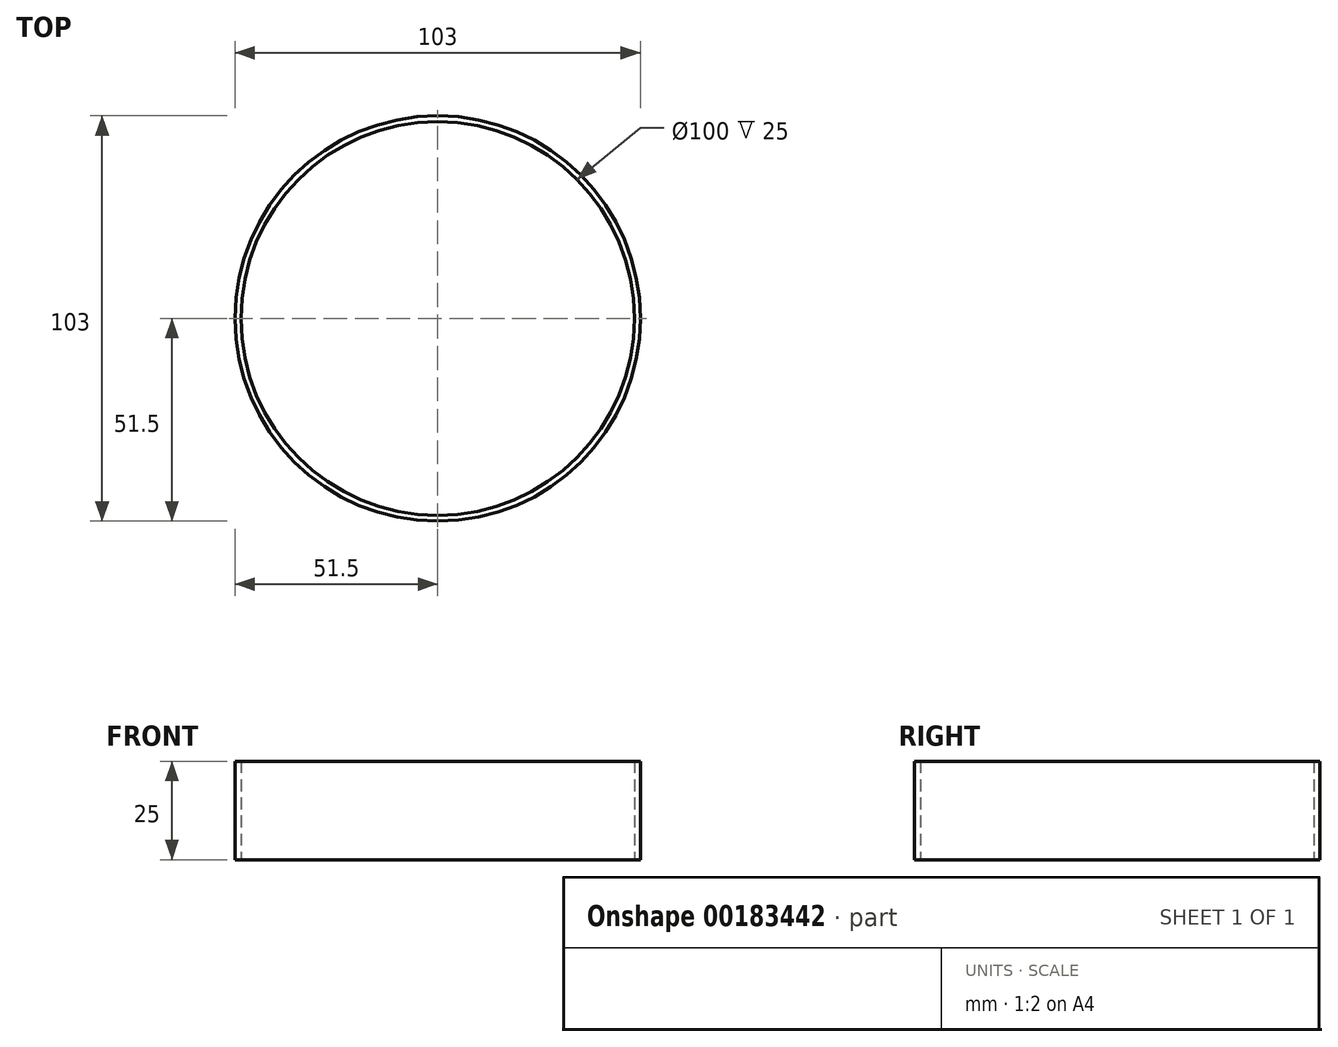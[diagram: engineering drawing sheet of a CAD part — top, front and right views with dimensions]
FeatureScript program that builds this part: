
annotation { "Feature Type Name" : "Feature", "Feature Type Description" : "" }
export const myFeature = defineFeature(function(context is Context, id is Id, definition is map)
    precondition{}
    {
        {
            var Q0;
            Q0=qCreatedBy(makeId("Top.planeOp"),FACE);
            var sketch = newSketch(context, id + "F0", { "sketchPlane" : qUnion([Q0])});
            skCircle(sketch, "E0", {"center": v(0, 0) * mm, "radius": 51.5 * mm});
            skCircle(sketch, "E1", {"center": v(0, 0) * mm, "radius": 50 * mm});
            skSolve(sketch);
        }
        {
            var Q0;
            Q0=makeQuery(id+"F0.imprint","IMPRINT",FACE,{"disambiguationData":[TD([[makeQuery(id+"F0.imprint","IMPRINT",EDGE,{"derivedFrom":sQuery(id+"F0.wireOp",EDGE,"E0")}),1.0]])]});
            extrude(context, id + "F1", {"entities" : qUnion([Q0]), "depth" : 25 * mm});
        }
    });
